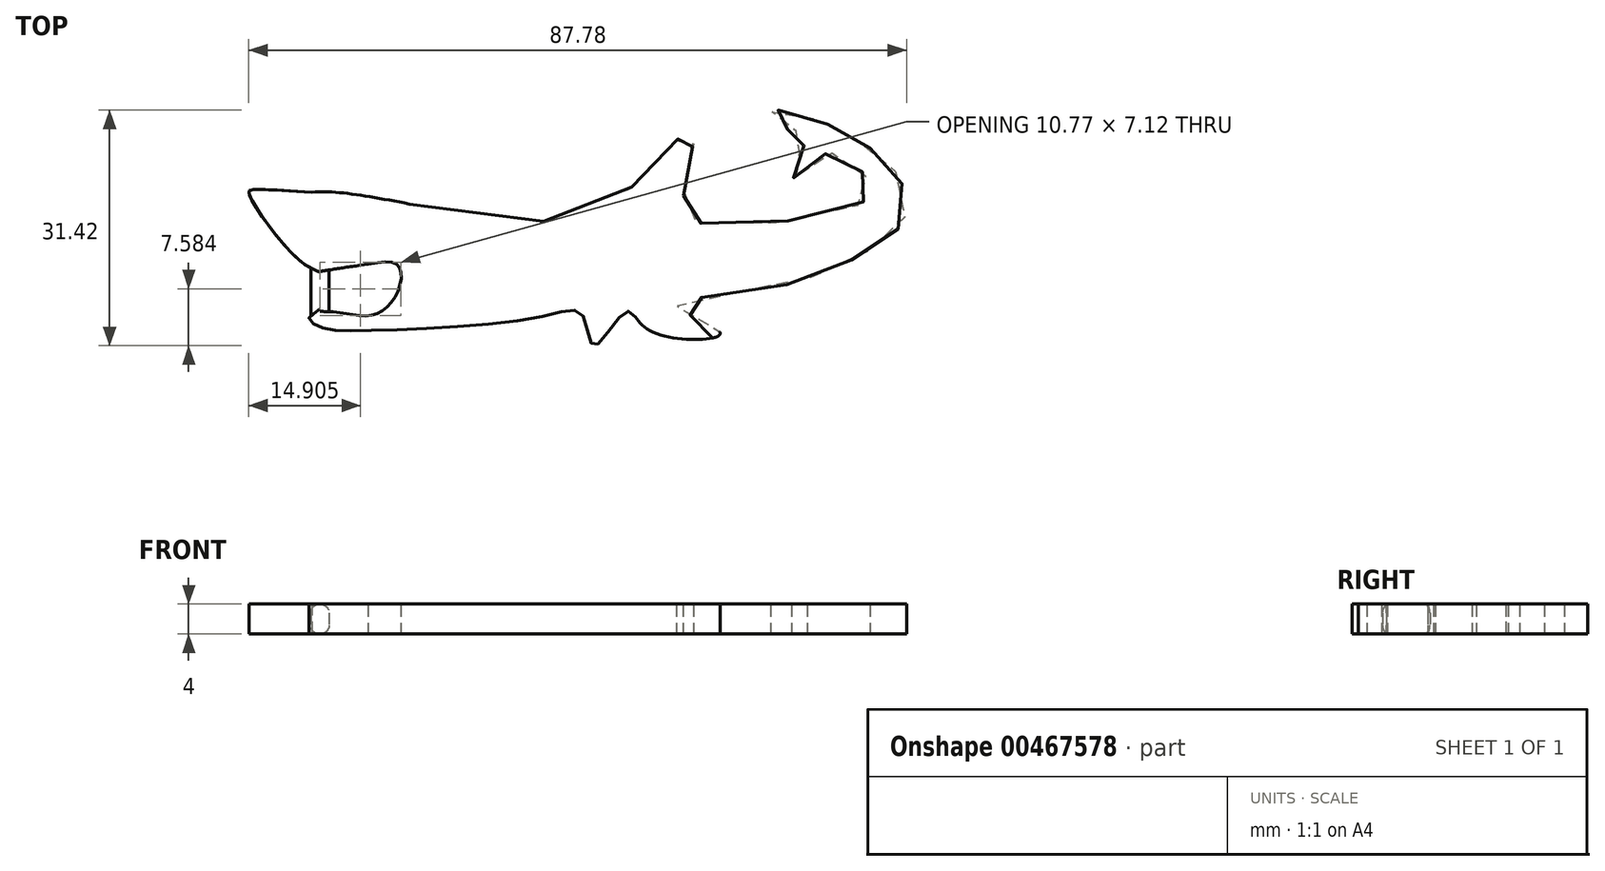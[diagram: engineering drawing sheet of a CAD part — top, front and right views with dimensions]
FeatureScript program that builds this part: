
annotation { "Feature Type Name" : "Feature", "Feature Type Description" : "" }
export const myFeature = defineFeature(function(context is Context, id is Id, definition is map)
    precondition{}
    {
        {
            var Q0;
            Q0=qCreatedBy(makeId("Top.planeOp"),FACE);
            var sketch = newSketch(context, id + "F0", { "sketchPlane" : qUnion([Q0])});
            skFitSpline(sketch, "E0", {"points": [v(-44.33, 24.45) * mm, v(-8.13, 21.75) * mm, v(6.18, 31.85) * mm, v(8.87, 33.2) * mm, v(8.54, 29.83) * mm, v(7.7, 23.27) * mm, v(9.88, 21.25) * mm, v(30.42, 23.44) * mm, v(32.61, 25.96) * mm, v(30.09, 29.5) * mm, v(25.54, 30.17) * mm, v(22.34, 27.3) * mm, v(22.85, 30.17) * mm, v(24.2, 32.86) * mm, v(20.66, 34.21) * mm, v(19.48, 36.06) * mm, v(24.7, 35.39) * mm, v(31.1, 32.19) * mm, v(35.98, 28.15) * mm, v(37.16, 21.92) * mm, v(31.43, 17.04) * mm, v(17.97, 12.32) * mm, v(6.85, 10.14) * mm, v(12.58, 6.6) * mm, v(3.15, 6.94) * mm, v(0, 9.46) * mm, v(-4.26, 4.92) * mm, v(-5.77, 8.96) * mm, v(-11.33, 8.79) * mm, v(-34.22, 6.94) * mm, v(-40.96, 7.44) * mm, v(-42.3, 8.62) * mm, v(-39.61, 9.46) * mm, v(-34.06, 8.96) * mm, v(-30.52, 11.99) * mm, v(-30.69, 15.86) * mm, v(-40.45, 16.03) * mm, v(-44.33, 24.45) * mm]});
            skFitSpline(sketch, "E1", {"points": [v(-34.35, 15.8) * mm, v(-39.15, 15.09) * mm, v(-42.95, 15.8) * mm, v(-50.29, 25.15) * mm, v(-50.12, 25.64) * mm, v(-47.81, 25.73) * mm, v(-41.9, 25.38) * mm], "startDerivative": vector(-28.43, -4.02) * mm, "endDerivative": vector(32.12, -2.02) * mm});
            skLineSegment(sketch, "E2", {"start": v(-41.9, 25.38) * mm, "end": v(-28.88, 23.82) * mm});
            skFitSpline(sketch, "E3", {"points": [v(1.25, 8.71) * mm, v(5.65, 6.96) * mm, v(11.55, 5.94) * mm], "startDerivative": vector(8.93, -4.14) * mm, "endDerivative": vector(11.62, -1.47) * mm});
            skLineSegment(sketch, "E4.left", {"start": v(-42.07, 15.27) * mm, "end": v(-42.07, 8.94) * mm});
            skLineSegment(sketch, "E4.right", {"start": v(-39.61, 15.02) * mm, "end": v(-39.61, 9.46) * mm});
            skPoint(sketch, "E5.orphan", {"position": v(-39.61, 5.53) * mm});
            skSolve(sketch);
        }
        {
            var Q0;
            Q0 = qSketchRegion(id + "F0", true);
            extrude(context, id + "F1", {"entities" : qUnion([Q0]), "depth" : 4 * mm});
        }
        {
            var Q0;
            Q0=makeQuery(id+"F1.opExtrude","CAP_EDGE",EDGE,{"disambiguationData":[OSD([sQuery(id+"F0.wireOp",EDGE,"E4.left")])],"isStart":false});
            var Q1;
            Q1=makeQuery(id+"F1.opExtrude","CAP_EDGE",EDGE,{"disambiguationData":[OSD([sQuery(id+"F0.wireOp",EDGE,"E4.right")])],"isStart":false});
            var Q2;
            Q2=makeQuery(id+"F1.opExtrude","CAP_EDGE",EDGE,{"disambiguationData":[OSD([sQuery(id+"F0.wireOp",EDGE,"E4.right")])],"isStart":true});
            var Q3;
            Q3=makeQuery(id+"F1.opExtrude","CAP_EDGE",EDGE,{"disambiguationData":[OSD([sQuery(id+"F0.wireOp",EDGE,"E4.left")])],"isStart":true});
            fillet(context, id + "F2", {"entities" : qUnion([Q0, Q1, Q2, Q3]), "radius" : 1.2 * mm, "tangentPropagation" : true, "allowEdgeOverflow" : false});
        }
    });
